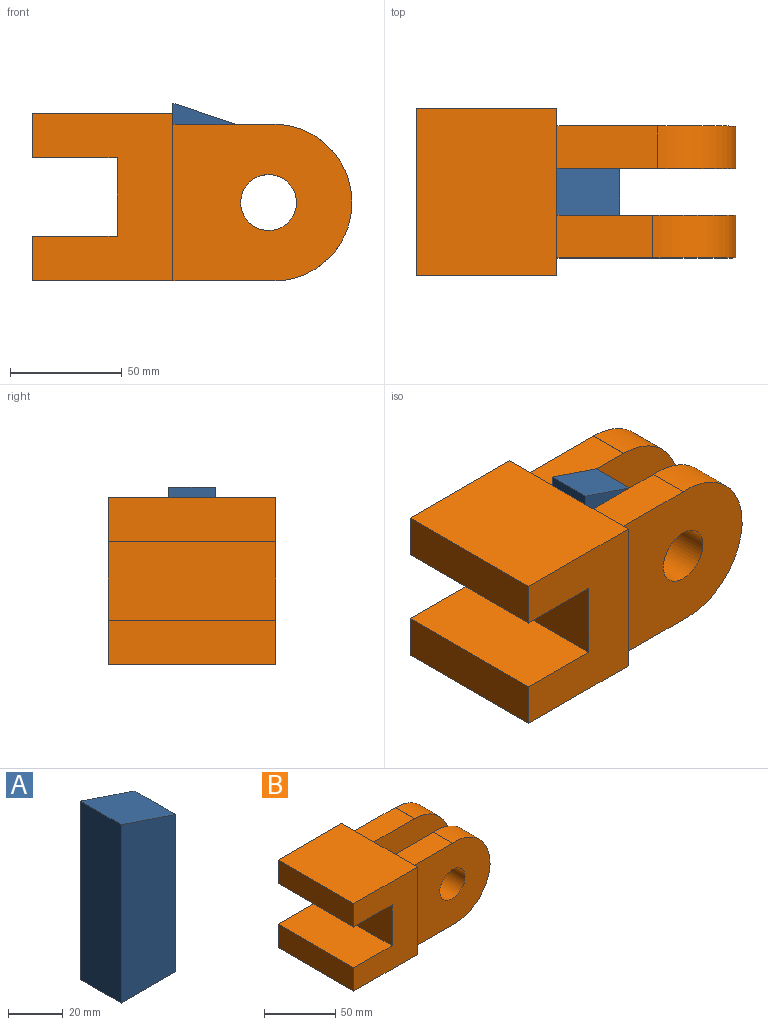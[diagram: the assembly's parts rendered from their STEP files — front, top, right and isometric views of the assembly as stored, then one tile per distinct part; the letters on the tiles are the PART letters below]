
ASSEMBLY  parts=2 mates=1
PART A: 6 faces, bbox 28x21x79.5 mm
  f0: plane 79.5x21mm, normal (-1,0,0), area 1669.5mm2, adj f1,f3,f4,f5
  f1: plane 79.5x28mm, normal (0,-1,0), area 2093.3mm2, adj f0,f2,f4,f5
  f2: plane 70.02x21mm, normal (1,0,0), area 1470.5mm2, adj f1,f3,f4,f5
  f3: plane 79.5x28mm, normal (0,1,0), area 2093.3mm2, adj f0,f2,f4,f5
  f4: plane 28x21mm, normal (0,0,-1), area 588mm2, adj f0,f1,f2,f3
  f5: plane 28x21mm, normal (0.32,0,0.95), area 620.8mm2, adj f0,f1,f2,f3
PART B: 22 faces, bbox 143.1x75x75.1 mm
  f0: plane 19x0.06mm, normal (1,0,0), area 1.1mm2, adj f7,f15,f16,f19
  f1: plane 75x75mm, normal (1,0,0), area 2965mm2, adj f3,f5,f6,f7,f11,f12,f13,f14
  f2: plane 75x20mm, normal (-1,0,0), area 1500mm2, adj f3,f5,f7,f8
  f3: plane 75x63mm, normal (0,-1,0), area 3395mm2, adj f1,f2,f4,f6,f7,f8,f9,f10
  f4: plane 75x20mm, normal (-1,0,0), area 1500mm2, adj f3,f5,f6,f10
  f5: plane 75x63mm, normal (0,1,0), area 3395mm2, adj f1,f2,f4,f6,f7,f8,f9,f10
  f6: plane 75x63mm, normal (0,0,1), area 4725mm2, adj f1,f3,f4,f5
  f7: plane 108x75mm, normal (0,0,-1), area 6392.7mm2, adj f0,f1,f2,f3,f5,f11,f13,f15
  f8: plane 75x38mm, normal (0,0,1), area 2850mm2, adj f2,f3,f5,f9
  f9: plane 75x35mm, normal (-1,0,0), area 2625mm2, adj f3,f5,f8,f10
  f10: plane 75x38mm, normal (0,0,-1), area 2850mm2, adj f3,f4,f5,f9
  f11: plane 80.07x70.14mm, normal (0,1,0), area 4591.3mm2, adj f1,f7,f12,f18,f21
  f12: plane 42.78x19mm, normal (0,0,1), area 812.7mm2, adj f1,f11,f13,f18
  f13: plane 80.07x70.14mm, normal (0,-1,0), area 4591.3mm2, adj f1,f7,f12,f18,f21
  f14: plane 45x19mm, normal (0,0,1), area 855mm2, adj f1,f15,f16,f17
  f15: plane 79.94x70mm, normal (0,-1,0), area 4576.9mm2, adj f0,f1,f7,f14,f17,f19,f20
  f16: plane 79.94x70mm, normal (0,1,0), area 4576.9mm2, adj f0,f1,f7,f14,f17,f19,f20
  f17: plane 19x0.06mm, normal (1,0,0), area 1.1mm2, adj f14,f15,f16,f19
  f18: cylinder r=35.07mm len=70.14mm, axis (0,-1,0), area 2178mm2, adj f7,f11,f12,f13
  f19: cylinder r=34.94mm len=69.88mm, axis (0,1,0), area 2085.7mm2, adj f0,f15,f16,f17
  f20: cylinder r=12.5mm len=25mm, axis (0,-1,0), area 1492.3mm2, adj f15,f16
  f21: cylinder r=12.5mm len=25mm, axis (0,-1,0), area 1492.3mm2, adj f11,f13
PLACE A t=(11.83,27.19,18.03)mm
PLACE B t=(-51.17,0.19,9.03)mm
MATE fastened A.f0 <-> B.f1  axis (-1,0,0) through (11.83,37.69,48.78)mm
